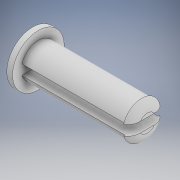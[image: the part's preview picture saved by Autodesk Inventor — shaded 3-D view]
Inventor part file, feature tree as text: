
AUTODESK INVENTOR PART (.ipt)
format: ipt  version: 2020 (Build 240168000, 168)  size: 136,704 bytes
history: native  units: mm
features: extrude x4, sketch x4, fillet x1
ambient origin geometry x8: Origin, YZ Plane, XZ Plane, XY Plane, X Axis, Y Axis, Z Axis, Center Point
bodies: Solid1 (feature_tree)
feature tree (9):
  extrude  "Extrusion1"  Depth=18.0mm TaperAngle=0.0deg
  extrude  "Extrusion2"  Depth=1.0mm TaperAngle=0.0deg
  extrude  "Extrusion3"  Depth=1.0mm TaperAngle=0.0deg
  extrude  "Extrusion4"  Depth=2.0mm
  fillet  "Fillet1"  [1 undecoded]
  sketch  "Sketch1"  dims[d0=6.0mm d1=18.0mm d2=0.0mm]
  sketch  "Sketch2"  dims[d3=9.0mm d4=1.0mm d5=0.0mm]
  sketch  "Sketch3"  dims[d6=6.5mm d7=1.0mm d8=0.0mm]
  sketch  "Sketch4"  dims[d9=19.0mm d10=0.0mm d11=2.0mm]
note: 1 required parameter value undecoded (feature->parameter linkage not recoverable at this tier; creation-order binding heuristic only, values carry confidence <= 0.55)
